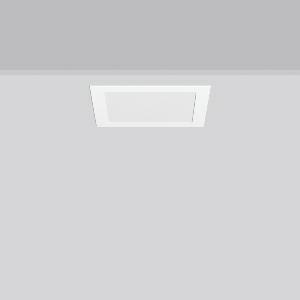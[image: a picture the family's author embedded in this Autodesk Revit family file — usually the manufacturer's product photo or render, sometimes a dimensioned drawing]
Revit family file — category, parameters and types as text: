
# Revit family: toledo_flat_square_e_672243_002_89_7792
name_source: partatom
category: Lighting Fixtures
units: mm (PartAtom-declared; Revit-internal decimal feet)

## family parameters
Cut with Voids When Loaded = No
Host = Face
Light Source = No
Part Type = Normal
Room Calculation Point = No
Round Connector Dimension = Use Diameter
Shared = No

## types (1)
- TOLEDO FLAT square E (1 x LED Modul 830, 1600 lm, 3000)
    Apparent Load = 19 VA
    CIE Flux Codes = 48 80 96 100 100
    Color Rendering = 80
    Color Temperature = 3000
    Default Elevation = 1800 mm
    Description = Series: TOLEDO FLAT square
Square recessed downlight. For escape route illumination. Housing: die-cast aluminium, powder-coated. Lightguide and diffuser made of non-yellowing plastic (PMMA). Diffuser opal matt plastic. Ceiling installation with spring system. Including separate LED converter with connecting cable 250 mm. Suitable for connection to central battery systems. With AC Control monitoring module for LUXIFAIR central battery units. External driver with simple plug-in locking system. 
Colour: white
Length: 225 mm
Width: 225 mm
Height: 3 mm
Cut-out length: 208 mm
Cut-out width: 208 mm
Recess height: 40 mm
Luminaire: recess height: 37-57 mm
Weight: 1.47 kg
Operating mode: maintained power mode
Lamp: LED
Socket: without socket
Colour temperature: 3000K
Colour rendering index (CRI): 80
System power: 19 W
Rated luminous flux: 1600 lm
Luminous flux, emergency: 1600 lm
System power, emergency: 19 W
Control gear: Regulated power supply
Protection class: I
Type of protection: IP 54
    Height = 0 mm  [stored 0 ft]
    Lamp = 1 x LED Modul 830
    Lamp Light Flux = 1600 lm
    Lamp count = 1
    Length = 225 mm
    Lifetime = 50000 h
    Luminous efficacy = 84 lm/W
    Manufacturer = RZB
    ModVariant = No
    Model = 672243.002.89
    Mounting Place = Ceiling
    Mounting Type = Recessed
    Number of Poles = 1
    OnlyDefault = Yes
    Power Factor = 1
    Product Name = TOLEDO FLAT square E
    Product group = Recessed downlights
    ProductGroupID = 402
    Protection Class = Protection class I
    Protection Degree = IP 40
    RLX_Detail_Level = 1
    RLX_Emergency_Light_Flux = 1600 lm
    RLX_Emergency_Type = 3
    RLX_Emergency_Type_DB = Yes
    RlxData = <blob elided: 11057 chars, md5=5dc2c602>
    Socket = socket
    Standby Power = 0 W
    System Light Flux = 1600 lm
    System Power = 19 W
    Type Comments = Product without accessories
    Type Image = 901487.002.jpg
    URL = http://relux.com
    VarID = ---
    Voltage = 230 V
    Voltage Range = 220-240 V
    Weight = 0.00 kg
    Width = 225 mm

note: [stored X ft] marks values corroborated as IEEE doubles in the binary element streams (Revit-internal decimal feet)

## geometry (parser evidence)
native form markers: Sweep x9
no freeform markers — native parametric forms only
